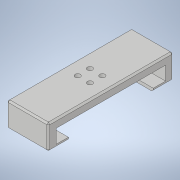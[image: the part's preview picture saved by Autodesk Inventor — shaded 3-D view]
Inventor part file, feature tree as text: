
AUTODESK INVENTOR PART (.ipt)
format: ipt  version: 2022 (Build 260153000, 153)  size: 154,624 bytes
history: native  units: in
note: dims shown in document units (in); Inventor stores cm internally (conversion verified against a paired STEP export)
features: sketch x3, extrude x2, hole x1, chamfer x1
ambient origin geometry x8: Origin, YZ Plane, XZ Plane, XY Plane, X Axis, Y Axis, Z Axis, Center Point
bodies: Solid1 (feature_tree)
feature tree (7):
  extrude  "Extrusion1"  Depth=1.063in
  extrude  "Extrusion2"  Depth=0.6299in
  hole  "Hole1"  [1 undecoded]
  chamfer  "Chamfer1"  Distance=0.1575in
  sketch  "Sketch1"  dims[d0=3.189in d1=1.063in]
  sketch  "Sketch2"  dims[d2=0.6299in d3=0.0in d4=0.1181in]
  sketch  "Sketch4"  dims[d5=0.1575in d6=0.1575in d7=0.1575in d8=0.1575in d9=0.1339in d10=0.339in d11=0.248in d12=0.25in d13=90.0deg d14=0.617in d15=0.8108in d28=0.0787in d29=0.315in d32=0.315in d33=0.1969in d35=0.0787in d37=0.0in d38=0.0in d39=0.1969in d40=0.1969in d41=0.0394in d42=0.0787in d43=45.0deg]
note: 1 required parameter value undecoded (feature->parameter linkage not recoverable at this tier; creation-order binding heuristic only, values carry confidence <= 0.55)
